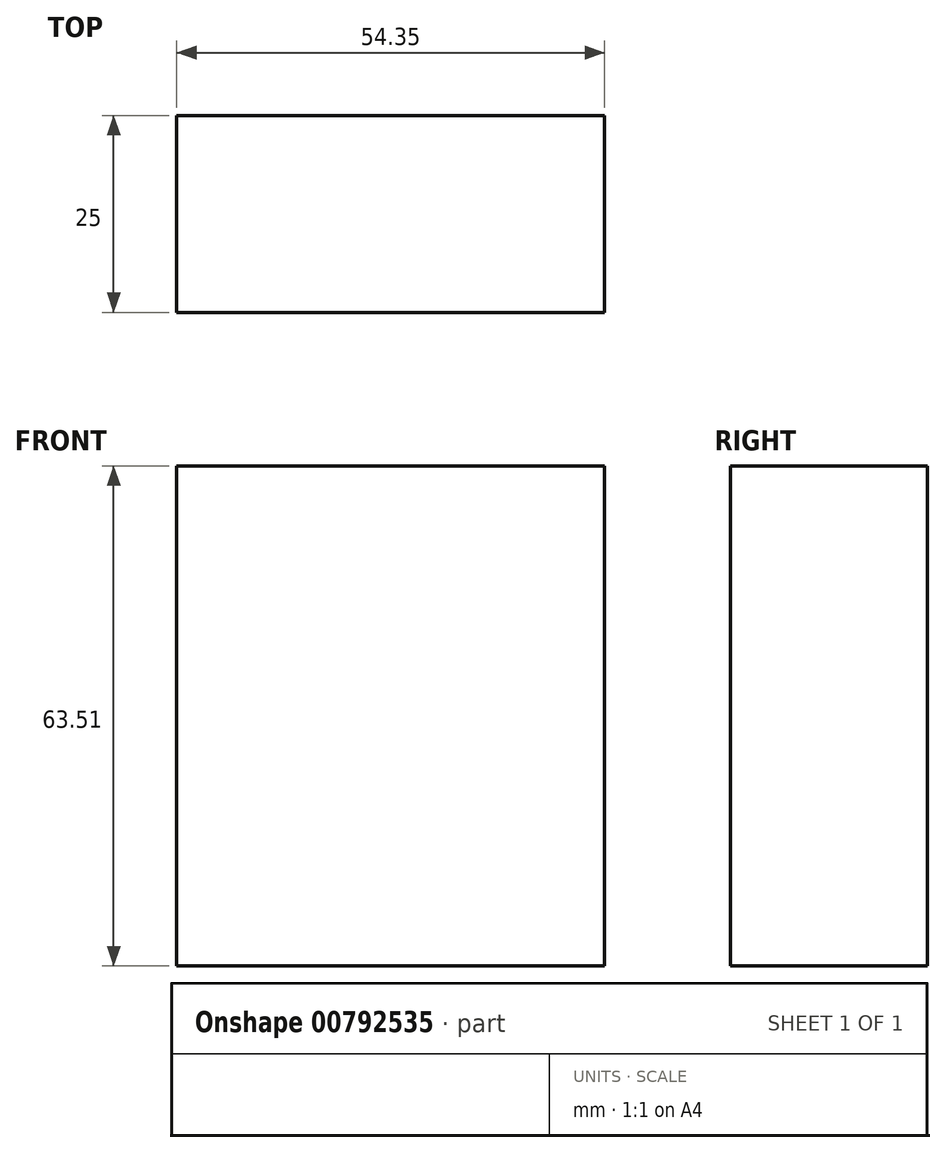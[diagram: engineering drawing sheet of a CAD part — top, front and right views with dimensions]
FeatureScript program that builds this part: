
annotation { "Feature Type Name" : "Feature", "Feature Type Description" : "" }
export const myFeature = defineFeature(function(context is Context, id is Id, definition is map)
    precondition{}
    {
        {
            var Q0;
            Q0=qCreatedBy(makeId("Front.planeOp"),FACE);
            var sketch = newSketch(context, id + "F0", { "sketchPlane" : qUnion([Q0])});
            skLineSegment(sketch, "E0.bottom", {"start": v(-129.31, 48.15) * mm, "end": v(-74.96, 48.15) * mm});
            skLineSegment(sketch, "E0.top", {"start": v(-129.31, -15.36) * mm, "end": v(-74.96, -15.36) * mm});
            skLineSegment(sketch, "E0.left", {"start": v(-129.31, 48.15) * mm, "end": v(-129.31, -15.36) * mm});
            skLineSegment(sketch, "E0.right", {"start": v(-74.96, 48.15) * mm, "end": v(-74.96, -15.36) * mm});
            skSolve(sketch);
        }
        {
            var Q0;
            Q0 = qSketchRegion(id + "F0", true);
            extrude(context, id + "F1", {"entities" : qUnion([Q0]), "depth" : 25 * mm, "offsetDistance" : 25 * mm});
        }
    });
